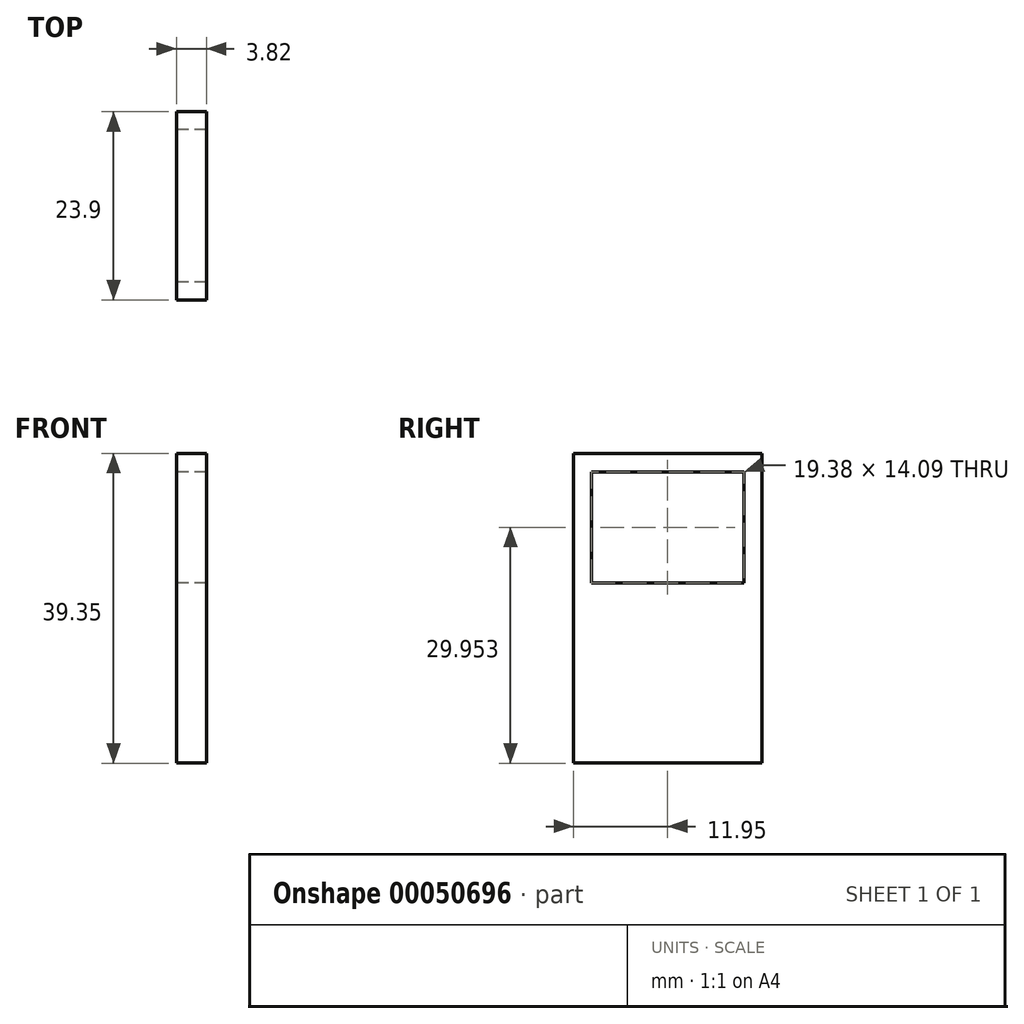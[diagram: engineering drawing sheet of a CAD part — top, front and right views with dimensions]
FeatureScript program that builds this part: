
annotation { "Feature Type Name" : "Feature", "Feature Type Description" : "" }
export const myFeature = defineFeature(function(context is Context, id is Id, definition is map)
    precondition{}
    {
        {
            var Q0;
            Q0=qCreatedBy(makeId("Right.planeOp"),FACE);
            var sketch = newSketch(context, id + "F0", { "sketchPlane" : qUnion([Q0])});
            skLineSegment(sketch, "E0.bottom", {"start": v(-11.95, 19.82) * mm, "end": v(11.95, 19.82) * mm});
            skLineSegment(sketch, "E0.right", {"start": v(11.95, 19.82) * mm, "end": v(11.95, -19.53) * mm});
            skLineSegment(sketch, "E0.left", {"start": v(-11.95, 19.82) * mm, "end": v(-11.95, -19.53) * mm});
            skLineSegment(sketch, "E0.top", {"start": v(-11.95, -19.53) * mm, "end": v(11.95, -19.53) * mm});
            skLineSegment(sketch, "E1.rect.bottom", {"start": v(-9.69, 17.47) * mm, "end": v(9.69, 17.47) * mm});
            skLineSegment(sketch, "E1.rect.top", {"start": v(-9.69, 3.38) * mm, "end": v(9.69, 3.38) * mm});
            skLineSegment(sketch, "E1.rect.left", {"start": v(-9.69, 17.47) * mm, "end": v(-9.69, 3.38) * mm});
            skLineSegment(sketch, "E1.rect.right", {"start": v(9.69, 17.47) * mm, "end": v(9.69, 3.38) * mm});
            skPoint(sketch, "E1.rect.middle", {"position": v(0, 10.42) * mm});
            skSolve(sketch);
        }
        {
            var Q0;
            Q0=makeQuery(id+"F0.imprint","IMPRINT",FACE,{"disambiguationData":[TD([[makeQuery(id+"F0.imprint","IMPRINT",EDGE,{"derivedFrom":sQuery(id+"F0.wireOp",EDGE,"E0.bottom")}),-1.0]])]});
            extrude(context, id + "F1", {"entities" : qUnion([Q0]), "endBound" : BoundingType.SYMMETRIC, "depth" : 3.8 * mm});
        }
        {
            var Q0;
            Q0=makeQuery(id+"F0.imprint","IMPRINT",FACE,{"disambiguationData":[TD([[makeQuery(id+"F0.imprint","IMPRINT",EDGE,{"derivedFrom":sQuery(id+"F0.wireOp",EDGE,"E1.rect.bottom")}),-1.0]])]});
            extrude(context, id + "F2", {"entities" : qUnion([Q0]), "endBound" : BoundingType.SYMMETRIC, "depth" : 3.8 * mm});
        }
    });
